# Revit family: F2AE_2963-2962-2606_OS275
name_source: partatom
category: Finestre
units: mm (PartAtom-declared; Revit-internal decimal feet)

## family parameters
Condiviso = No
Host = Muro
Numero OmniClass = 23.30.20.00
Punto di calcolo locali = No
Sempre verticale = Sì
Taglio con vuoti quando caricato = No
Titolo OmniClass = Windows

## types (4) — shared parameters
Altezza di default del davanzale = 800 mm
Chiusura muro = Per host
Costruzione analitica = <Nessuno>
Descrizione = Finestra 2 ante battente apertura eterna
H_Max = 2900 mm
H_Min = 300 mm
L_Max = 2000 mm  [stored 6.56168 ft]
L_Min = 600 mm
Maniglia_alta = 1050 mm  [stored 3.44488 ft]
Maniglia_media = 500 mm  [stored 1.64042 ft]
Modello = OS2 75
Produttore = Secco Sistemi Spa
URL = https://www.seccosistemi.com
WARNING = No
n2_cerniere = 2
n3_cerniere = 3
n4_cerniere = 4
numero_cerniere = 3

## per-type parameters (varying)
| type | Altezza | H | H1 | H_man | H_maniglia | H_vetro | L | L1 | L_vetro | Larghezza | Larghezza_1A | Larghezza_2A | MATERIALE | Maniglia_bassa |
| Acciao Corten | 1500 mm | 1500 mm | 1500 mm | 500 mm  [stored 1.64042 ft] | 500 mm  [stored 1.64042 ft] | 1424 mm | 1000 mm  [stored 3.28084 ft] | 1000 mm  [stored 3.28084 ft] | 440 mm | 1000 mm  [stored 3.28084 ft] | 516 mm | 516 mm | Acciaio corten | 750 mm |
| Acciaio inox | 1500 mm | 1500 mm | 1500 mm | 500 mm  [stored 1.64042 ft] | 500 mm  [stored 1.64042 ft] | 1424 mm | 1200 mm | 1200 mm | 540 mm | 1200 mm | 616 mm | 616 mm | Acciaio inox, spazzolato | 750 mm |
| Acciaio zincato | 1500 mm | 1500 mm | 1500 mm | 500 mm  [stored 1.64042 ft] | 500 mm  [stored 1.64042 ft] | 1424 mm | 1000 mm  [stored 3.28084 ft] | 1000 mm  [stored 3.28084 ft] | 440 mm | 1000 mm  [stored 3.28084 ft] | 516 mm | 516 mm | Acciaio | 750 mm |
| Ottone | 2000 mm  [stored 6.56168 ft] | 2000 mm  [stored 6.56168 ft] | 2000 mm  [stored 6.56168 ft] | 1050 mm  [stored 3.44488 ft] | 1050 mm  [stored 3.44488 ft] | 1924 mm  [stored 6.31234 ft] | 2000 mm  [stored 6.56168 ft] | 2000 mm  [stored 6.56168 ft] | 940 mm  [stored 3.08399 ft] | 2000 mm  [stored 6.56168 ft] | 1016 mm | 1016 mm | Ottone | 1000 mm  [stored 3.28084 ft] |

note: [stored X ft] marks values corroborated as IEEE doubles in the binary element streams (Revit-internal decimal feet)
